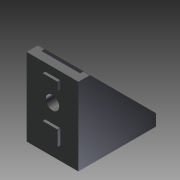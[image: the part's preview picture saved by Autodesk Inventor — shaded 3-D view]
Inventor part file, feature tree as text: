
AUTODESK INVENTOR PART (.ipt)
format: ipt  version: 2011 SP1 (Build 150282100, 282)  size: 159,232 bytes
history: native  units: mm
features: other x42, sketch x8, extrude x5, hole x3
ambient origin geometry x8: Origin, YZ Plane, XZ Plane, XY Plane, X Axis, Y Axis, Z Axis, Center Point
bodies: Solid1 (feature_tree)
feature tree (58):
  extrude  "Extrusion1"  Depth=15.0mm TaperAngle=0.0deg
  extrude  "Extrusion2"  Depth=1.0mm TaperAngle=0.0deg
  extrude  "Extrusion3"  TaperAngle=0.0deg  [1 undecoded]
  hole  "Hole1"  [1 undecoded]
  hole  "Hole2"  [1 undecoded]
  hole  "Hole3"  [1 undecoded]
  extrude  "Extrusion4"  [1 undecoded]
  extrude  "Extrusion5"  [1 undecoded]
  other  "bracket_to_bolt_XY"
  other  "bracket_to_bolt_YZ"
  other  "bracket_to_bolt_ZX"
  other  "bracket_to_bolt_X"
  other  "bracket_to_bolt_Y"
  other  "bracket_to_bolt_Z"
  other  "bracket_to_bolt_Center"
  other  "bracket_to_dummy_XY"
  other  "bracket_to_dummy_YZ"
  other  "bracket_to_dummy_ZX"
  other  "bracket_to_dummy_X"
  other  "bracket_to_dummy_Y"
  other  "bracket_to_dummy_Z"
  other  "bracket_to_dummy_Center"
  other  "to_bolt_4_7_base_XY"
  other  "to_bolt_4_7_base_YZ"
  other  "to_bolt_4_7_base_ZX"
  other  "to_bolt_4_7_base_X"
  other  "to_bolt_4_7_base_Y"
  other  "to_bolt_4_7_base_Z"
  other  "to_bolt_4_7_base_Center"
  other  "to_bolt_row_4_to_7_XY"
  other  "to_bolt_row_4_to_7_YZ"
  other  "to_bolt_row_4_to_7_ZX"
  other  "to_bolt_row_4_to_7_X"
  other  "to_bolt_row_4_to_7_Y"
  other  "to_bolt_row_4_to_7_Z"
  other  "to_bolt_row_4_to_7_Center"
  other  "to_nut_base_4_7_XY"
  other  "to_nut_base_4_7_YZ"
  other  "to_nut_base_4_7_ZX"
  other  "to_nut_base_4_7_X"
  other  "to_nut_base_4_7_Y"
  other  "to_nut_base_4_7_Z"
  other  "to_nut_base_4_7_Center"
  other  "to_nut_row_4_to_7_XY"
  other  "to_nut_row_4_to_7_YZ"
  other  "to_nut_row_4_to_7_ZX"
  other  "to_nut_row_4_to_7_X"
  other  "to_nut_row_4_to_7_Y"
  other  "to_nut_row_4_to_7_Z"
  other  "to_nut_row_4_to_7_Center"
  sketch  "Sketch_15"  dims[d29=1.0mm d30=0.0mm d31=0.0mm d32=0.0mm]
  sketch  "Sketch_16"
  sketch  "Sketch_17"
  sketch  "Sketch4"  dims[d4=2.25mm d5=0.0mm]
  sketch  "Sketch5"  dims[d13=5.2mm d14=6.0mm d15=4.0mm d16=2.0mm d17=90.0deg d18=4.5mm d19=0.0mm]
  sketch  "Sketch6"  dims[d20=5.2mm d21=6.0mm d22=4.0mm d23=2.0mm d24=90.0deg d25=4.5mm d26=0.0mm d27=1.0mm d28=0.0mm]
  sketch  "Sketch_1"  dims[d0=20.0mm d1=0.0mm d2=15.0mm d3=0.0mm]
  sketch  "Sketch_4"  dims[d6=5.2mm d7=6.0mm d8=4.0mm d9=2.0mm d10=90.0deg d11=4.5mm d12=0.0mm]
note: 6 required parameter values undecoded (feature->parameter linkage not recoverable at this tier; creation-order binding heuristic only, values carry confidence <= 0.55)
